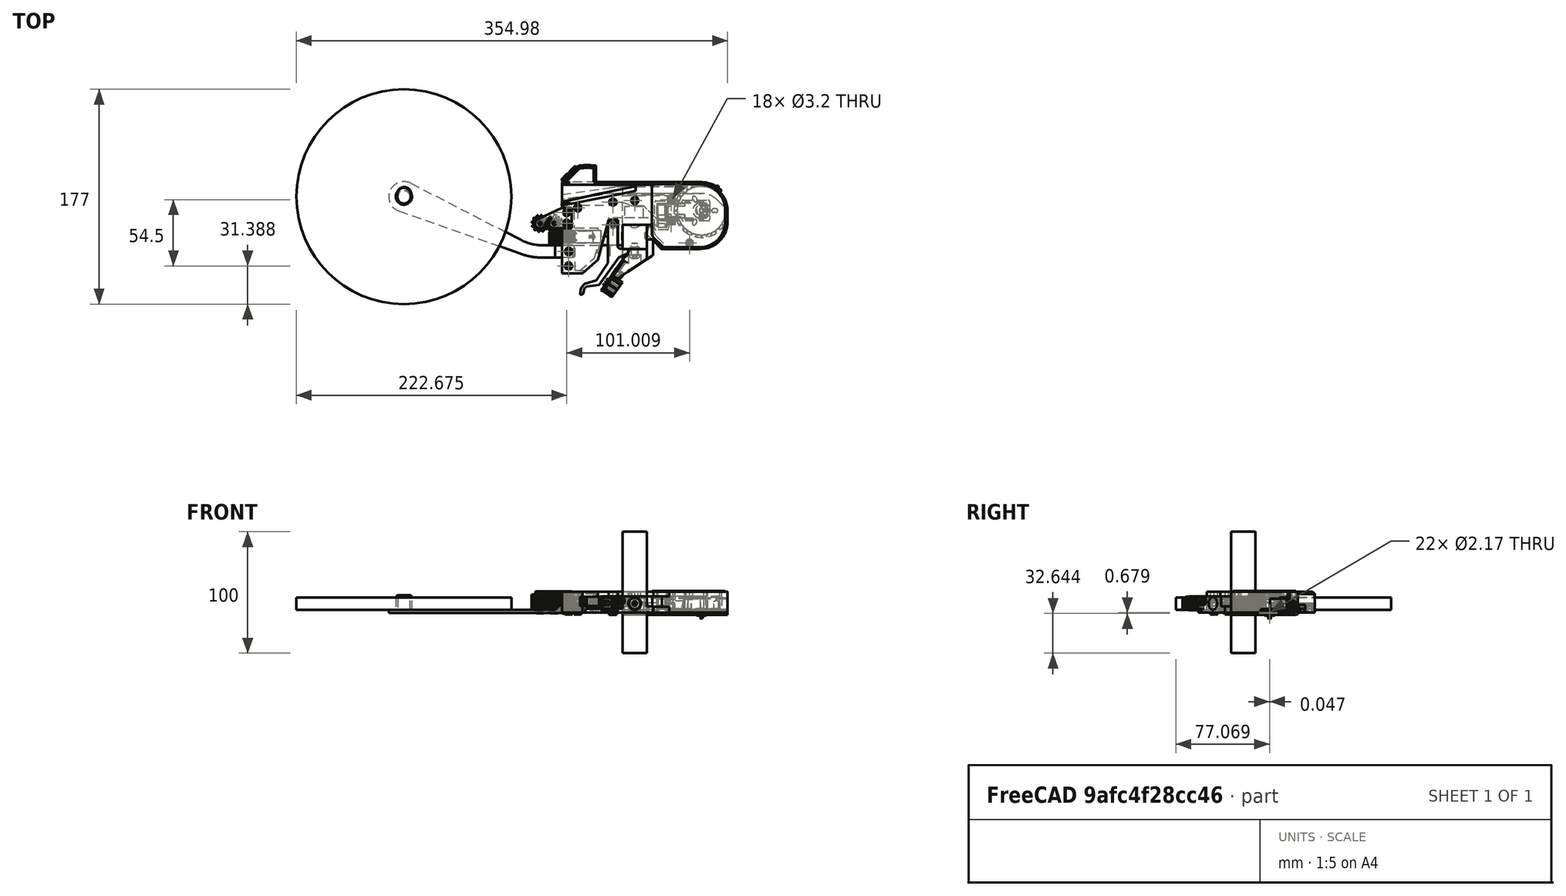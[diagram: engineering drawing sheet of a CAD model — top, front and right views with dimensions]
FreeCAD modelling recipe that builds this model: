
FCSTD DOCUMENT  (FreeCAD 0.20R29603 (Git))
Label: asm
License: All rights reserved
LicenseURL: http://en.wikipedia.org/wiki/All_rights_reserved
objects: Part::FeaturePython×80, PartDesign::CoordinateSystem×29, App::Part×1
note: 109 computed .brp shape members not serialized (recipe doc carries the construction recipe); baked Part::Feature solids carry a one-line shape summary decoded from their .brp

FEATURE [Part::FeaturePython] b_rail_001_  label="rail_Body_001"  # a2plus imported part (geometry in sourceFile) (typed FeaturePython)
  Placement = pos=(132.29,-99.02,-33.33) rot=(-1,0,0;1.5708rad)
  a2p_Version = V0.1
  fixedPosition = true
  objectType = a2pPart
  sourceFile = ./rail.FCStd
  sourcePart = Body
  subassemblyImport = false
  timeLastImport = 1.65956e+09
  updateColors = true
FEATURE [PartDesign::CoordinateSystem] a2pLCS
  AttacherType = Attacher::AttachEngine3D
FEATURE [Part::FeaturePython] b_LCS_Collection_  label="LCS_Collection"  # WARN: FeaturePython — macro-defined, semantics opaque (R4)
  Group = -> [a2pLCS]
  Owner = b_feederFloorPCB_001_
  Placement = pos=(148.005,-87.9308,34.6832) rot=(0.287968,0.913318,-0.287968;1.66134rad)
FEATURE [Part::FeaturePython] b_feederFloorPCB_001_  label="feederFloorPCB_001"  # a2plus imported part (geometry in sourceFile) (typed FeaturePython)
  Placement = pos=(148.005,-87.9308,34.6832) rot=(0.287968,0.913318,-0.287968;1.66134rad)
  a2p_Version = V0.1
  fixedPosition = false
  lcsLink = -> [b_LCS_Collection_]
  objectType = a2pPart
  sourceFile = ./feederFloorPCB.FCStd
  subassemblyImport = false
  timeLastImport = 1.67053e+09
  updateColors = true
FEATURE [Part::FeaturePython] b_frame_001_  label="frame_Body_001"  # a2plus imported part (geometry in sourceFile) (typed FeaturePython)
  Placement = pos=(132.339,-79.0017,-1.65661) rot=(-1,0,0;1.5708rad)
  a2p_Version = 0.4.60i
  fixedPosition = false
  objectType = a2pPart
  sourceFile = ./frame.FCStd
  sourcePart = Body
  subassemblyImport = false
  timeLastImport = 1.68014e+09
  updateColors = true
FEATURE [Part::FeaturePython] b_railLock_001_  label="railLock_Body_001"  # a2plus imported part (geometry in sourceFile) (typed FeaturePython)
  Placement = pos=(128.216,-75.0366,5.45816) rot=(-1,0,0;1.5708rad)
  a2p_Version = V0.1
  fixedPosition = false
  objectType = a2pPart
  sourceFile = ./railLock.FCStd
  sourcePart = Body
  subassemblyImport = false
  timeLastImport = 1.66559e+09
  updateColors = true
FEATURE [Part::FeaturePython] Screw  label="M5x10-Screw"  # Fasteners workbench fastener (typed FeaturePython)
  Placement = pos=(142.2,-104.2,7.5) rot=(1,0,0;1.5708rad)
  diameter = 3
  invert = false
  leftHanded = false
  length = 1
  lengthCustom = 10
  matchOuter = false
  offset = 0
  thread = false
  type = 40
FEATURE [PartDesign::CoordinateSystem] a2pLCS022
  AttacherType = Attacher::AttachEngine3D
FEATURE [Part::FeaturePython] b_LCS_Collection_022  label="LCS_Collection022"  # WARN: FeaturePython — macro-defined, semantics opaque (R4)
  Group = -> [a2pLCS022]
  Owner = b_controllerPCB_001_
  Placement = pos=(0.0377435,-0.00241684,-0.0301529) rot=(0,0,1;0rad)
FEATURE [Part::FeaturePython] b_controllerPCB_001_  label="controllerPCB_001"  # a2plus imported part (geometry in sourceFile) (typed FeaturePython)
  Placement = pos=(0.0377435,-0.00241684,-0.0301529) rot=(0,0,1;0rad)
  a2p_Version = V0.1
  fixedPosition = false
  lcsLink = -> [b_LCS_Collection_022]
  objectType = a2pPart
  sourceFile = ./controllerPCB.FCStd
  subassemblyImport = false
  timeLastImport = 1.67242e+09
  updateColors = true
FEATURE [App::Part] Part
  Group = -> [b_LCS_Collection_022,b_controllerPCB_001_,b_frame_001_]
  Origin = -> Origin
FEATURE [PartDesign::CoordinateSystem] a2pLCS023
  AttacherType = Attacher::AttachEngine3D
FEATURE [Part::FeaturePython] b_LCS_Collection_023  label="LCS_Collection023"  # WARN: FeaturePython — macro-defined, semantics opaque (R4)
  Group = -> [a2pLCS023]
  Owner = CachedObject_0
FEATURE [Part::FeaturePython] b_feeder_floor_001_001  label="feeder-floor_Body_001"  # a2plus imported part (geometry in sourceFile) (typed FeaturePython)
  Placement = pos=(152.293,-99.0214,-0.00814896) rot=(0,0,1;0rad)
  a2p_Version = V0.1
  fixedPosition = false
  objectType = a2pPart
  sourceFile = ./feeder-floor.FCStd
  sourcePart = Body
  subassemblyImport = false
  timeLastImport = 1.67053e+09
  updateColors = true
FEATURE [PartDesign::CoordinateSystem] a2pLCS024
  AttacherType = Attacher::AttachEngine3D
FEATURE [Part::FeaturePython] b_LCS_Collection_024  label="LCS_Collection024"  # WARN: FeaturePython — macro-defined, semantics opaque (R4)
  Group = -> [a2pLCS024]
  Owner = CachedObject_0
FEATURE [PartDesign::CoordinateSystem] a2pLCS025
  AttacherType = Attacher::AttachEngine3D
FEATURE [Part::FeaturePython] b_LCS_Collection_025  label="LCS_Collection025"  # WARN: FeaturePython — macro-defined, semantics opaque (R4)
  Group = -> [a2pLCS025]
  Owner = CachedObject_0
FEATURE [PartDesign::CoordinateSystem] a2pLCS026
  AttacherType = Attacher::AttachEngine3D
FEATURE [Part::FeaturePython] b_LCS_Collection_026  label="LCS_Collection026"  # WARN: FeaturePython — macro-defined, semantics opaque (R4)
  Group = -> [a2pLCS026]
  Owner = CachedObject_0
FEATURE [PartDesign::CoordinateSystem] a2pLCS027
  AttacherType = Attacher::AttachEngine3D
FEATURE [Part::FeaturePython] b_LCS_Collection_027  label="LCS_Collection027"  # WARN: FeaturePython — macro-defined, semantics opaque (R4)
  Group = -> [a2pLCS027]
  Owner = CachedObject_0
FEATURE [PartDesign::CoordinateSystem] a2pLCS028
  AttacherType = Attacher::AttachEngine3D
FEATURE [Part::FeaturePython] b_LCS_Collection_028  label="LCS_Collection028"  # WARN: FeaturePython — macro-defined, semantics opaque (R4)
  Group = -> [a2pLCS028]
  Owner = CachedObject_0
FEATURE [Part::FeaturePython] Nut  label="M3-Nut"  # Fasteners workbench fastener (typed FeaturePython)
  Placement = pos=(129.317,-119.93,9.48) rot=(0.287968,0.913318,-0.287968;1.66134rad)
  diameter = 4
  invert = false
  leftHanded = false
  matchOuter = false
  offset = 0
  thread = false
  type = 7
FEATURE [PartDesign::CoordinateSystem] a2pLCS029
  AttacherType = Attacher::AttachEngine3D
FEATURE [Part::FeaturePython] b_LCS_Collection_029  label="LCS_Collection029"  # WARN: FeaturePython — macro-defined, semantics opaque (R4)
  Group = -> [a2pLCS029]
  Owner = CachedObject_0
FEATURE [PartDesign::CoordinateSystem] a2pLCS030
  AttacherType = Attacher::AttachEngine3D
FEATURE [Part::FeaturePython] b_LCS_Collection_030  label="LCS_Collection030"  # WARN: FeaturePython — macro-defined, semantics opaque (R4)
  Group = -> [a2pLCS030]
  Owner = CachedObject_0
FEATURE [PartDesign::CoordinateSystem] a2pLCS031
  AttacherType = Attacher::AttachEngine3D
FEATURE [Part::FeaturePython] b_LCS_Collection_031  label="LCS_Collection031"  # WARN: FeaturePython — macro-defined, semantics opaque (R4)
  Group = -> [a2pLCS031]
  Owner = CachedObject_0
FEATURE [PartDesign::CoordinateSystem] a2pLCS032
  AttacherType = Attacher::AttachEngine3D
FEATURE [Part::FeaturePython] b_LCS_Collection_032  label="LCS_Collection032"  # WARN: FeaturePython — macro-defined, semantics opaque (R4)
  Group = -> [a2pLCS032]
  Owner = CachedObject_0
FEATURE [PartDesign::CoordinateSystem] a2pLCS033
  AttacherType = Attacher::AttachEngine3D
FEATURE [Part::FeaturePython] b_LCS_Collection_033  label="LCS_Collection033"  # WARN: FeaturePython — macro-defined, semantics opaque (R4)
  Group = -> [a2pLCS033]
  Owner = CachedObject_0
FEATURE [PartDesign::CoordinateSystem] a2pLCS034
  AttacherType = Attacher::AttachEngine3D
FEATURE [Part::FeaturePython] b_LCS_Collection_034  label="LCS_Collection034"  # WARN: FeaturePython — macro-defined, semantics opaque (R4)
  Group = -> [a2pLCS034]
  Owner = CachedObject_0
FEATURE [PartDesign::CoordinateSystem] a2pLCS035
  AttacherType = Attacher::AttachEngine3D
FEATURE [Part::FeaturePython] b_LCS_Collection_035  label="LCS_Collection035"  # WARN: FeaturePython — macro-defined, semantics opaque (R4)
  Group = -> [a2pLCS035]
  Owner = CachedObject_0
FEATURE [PartDesign::CoordinateSystem] a2pLCS036
  AttacherType = Attacher::AttachEngine3D
FEATURE [Part::FeaturePython] b_LCS_Collection_036  label="LCS_Collection036"  # WARN: FeaturePython — macro-defined, semantics opaque (R4)
  Group = -> [a2pLCS036]
  Owner = CachedObject_0
FEATURE [Part::FeaturePython] b_spool_holder_001_  label="spool-holder_Body_001"  # a2plus imported part (geometry in sourceFile) (typed FeaturePython)
  Placement = pos=(92.2739,-106.017,2.19804) rot=(0,0,1;0rad)
  a2p_Version = V0.1
  fixedPosition = false
  objectType = a2pPart
  sourceFile = ./spool-holder.FCStd
  sourcePart = Body
  subassemblyImport = false
  timeLastImport = 1.67476e+09
  updateColors = true
FEATURE [Part::FeaturePython] b_spool_001_  label="spool_Body_001"  # a2plus imported part (geometry in sourceFile) (typed FeaturePython)
  Placement = pos=(-47.8234,-55.8871,2.36078) rot=(0,0,1;0rad)
  a2p_Version = V0.1
  fixedPosition = false
  objectType = a2pPart
  sourceFile = ./spool.FCStd
  sourcePart = Body
  subassemblyImport = false
  timeLastImport = 1.66558e+09
  updateColors = true
FEATURE [Part::FeaturePython] b_film_gear_frame_001_001  label="film-gear-frame_Body_002"  # a2plus imported part (geometry in sourceFile) (typed FeaturePython)
  Placement = pos=(64.3546,-77.9852,17.3599) rot=(0.57735,0.57735,0.57735;4.18879rad)
  a2p_Version = 0.4.60i
  fixedPosition = false
  objectType = a2pPart
  sourceFile = ./film-gear-frame.FCStd
  sourcePart = Body
  subassemblyImport = false
  timeLastImport = 1.68013e+09
  updateColors = true
FEATURE [Part::FeaturePython] b_drive_motor_bracket_001_  label="drive-motor-bracket_Body_001"  # a2plus imported part (geometry in sourceFile) (typed FeaturePython)
  Placement = pos=(175.069,-78.8015,1.90918) rot=(0.707107,0.707107,0;3.14159rad)
  a2p_Version = V0.1
  fixedPosition = false
  objectType = a2pPart
  sourceFile = ./drive-motor-bracket.FCStd
  sourcePart = Body
  subassemblyImport = false
  timeLastImport = 1.67476e+09
  updateColors = true
FEATURE [Part::FeaturePython] b_drive_motor_cover_001_  label="drive-motor-cover_Body_001"  # a2plus imported part (geometry in sourceFile) (typed FeaturePython)
  Placement = pos=(132.364,-79.0154,-1.70701) rot=(-1,0,0;1.5708rad)
  a2p_Version = V0.1
  fixedPosition = false
  objectType = a2pPart
  sourceFile = ./drive-motor-cover.FCStd
  sourcePart = Body
  subassemblyImport = false
  timeLastImport = 1.67475e+09
  updateColors = true
FEATURE [Part::FeaturePython] b_right_angle_n20_001_  label="right-angle-n20_Body_001"  # a2plus imported part (geometry in sourceFile) (typed FeaturePython)
  Placement = pos=(197.308,-67.2968,3.38748) rot=(0.707107,0.707107,0;3.14159rad)
  a2p_Version = V0.1
  fixedPosition = false
  objectType = a2pPart
  sourceFile = ./right-angle-n20.FCStd
  sourcePart = Body
  subassemblyImport = false
  timeLastImport = 1.6668e+09
  updateColors = true
FEATURE [Part::FeaturePython] b_peel_gear_001_  label="peel-gear_Body_001"  # a2plus imported part (geometry in sourceFile) (typed FeaturePython)
  Placement = pos=(75.8569,-77.9542,14.8915) rot=(0.034899,0.999391,0;3.14159rad)
  a2p_Version = 0.4.60i
  fixedPosition = false
  objectType = a2pPart
  sourceFile = ./peel-gear.FCStd
  sourcePart = Body
  subassemblyImport = false
  timeLastImport = 1.68013e+09
  updateColors = true
FEATURE [Part::FeaturePython] b_peel_gear_001_001  label="peel-gear_Body_002"  # a2plus imported part (geometry in sourceFile) (typed FeaturePython)
  Placement = pos=(64.342,-77.973,14.939) rot=(0.087156,0.996195,0;3.14159rad)
  a2p_Version = 0.4.60i
  fixedPosition = false
  objectType = a2pPart
  sourceFile = ./peel-gear.FCStd
  sourcePart = Body
  subassemblyImport = false
  timeLastImport = 1.68013e+09
  updateColors = true
FEATURE [PartDesign::CoordinateSystem] a2pLCS037
  AttacherType = Attacher::AttachEngine3D
FEATURE [Part::FeaturePython] b_LCS_Collection_037  label="LCS_Collection037"  # WARN: FeaturePython — macro-defined, semantics opaque (R4)
  Group = -> [a2pLCS037]
  Owner = CachedObject_1
FEATURE [PartDesign::CoordinateSystem] a2pLCS038
  AttacherType = Attacher::AttachEngine3D
FEATURE [Part::FeaturePython] b_LCS_Collection_038  label="LCS_Collection038"  # WARN: FeaturePython — macro-defined, semantics opaque (R4)
  Group = -> [a2pLCS038]
  Owner = CachedObject_0
FEATURE [PartDesign::CoordinateSystem] a2pLCS039
  AttacherType = Attacher::AttachEngine3D
FEATURE [Part::FeaturePython] b_LCS_Collection_039  label="LCS_Collection039"  # WARN: FeaturePython — macro-defined, semantics opaque (R4)
  Group = -> [a2pLCS039]
  Owner = CachedObject_1
FEATURE [Part::FeaturePython] b_diffusor_001_  label="diffusor_Body_001"  # a2plus imported part (geometry in sourceFile) (typed FeaturePython)
  Placement = pos=(100.03,-30.0449,-0.0241241) rot=(0,0,1;0rad)
  a2p_Version = V0.1
  fixedPosition = false
  objectType = a2pPart
  sourceFile = ./diffusor.FCStd
  sourcePart = Body
  subassemblyImport = false
  timeLastImport = 1.67001e+09
  updateColors = true
FEATURE [PartDesign::CoordinateSystem] a2pLCS040
  AttacherType = Attacher::AttachEngine3D
FEATURE [Part::FeaturePython] b_LCS_Collection_040  label="LCS_Collection040"  # WARN: FeaturePython — macro-defined, semantics opaque (R4)
  Group = -> [a2pLCS040]
  Owner = CachedObject_0
FEATURE [PartDesign::CoordinateSystem] a2pLCS041
  AttacherType = Attacher::AttachEngine3D
FEATURE [Part::FeaturePython] b_LCS_Collection_041  label="LCS_Collection041"  # WARN: FeaturePython — macro-defined, semantics opaque (R4)
  Group = -> [a2pLCS041]
  Owner = CachedObject_0
FEATURE [PartDesign::CoordinateSystem] a2pLCS042
  AttacherType = Attacher::AttachEngine3D
FEATURE [Part::FeaturePython] b_LCS_Collection_042  label="LCS_Collection042"  # WARN: FeaturePython — macro-defined, semantics opaque (R4)
  Group = -> [a2pLCS042]
  Owner = CachedObject_0
FEATURE [PartDesign::CoordinateSystem] a2pLCS043
  AttacherType = Attacher::AttachEngine3D
FEATURE [Part::FeaturePython] b_LCS_Collection_043  label="LCS_Collection043"  # WARN: FeaturePython — macro-defined, semantics opaque (R4)
  Group = -> [a2pLCS043]
  Owner = CachedObject_0
FEATURE [PartDesign::CoordinateSystem] a2pLCS044
  AttacherType = Attacher::AttachEngine3D
FEATURE [Part::FeaturePython] b_LCS_Collection_044  label="LCS_Collection044"  # WARN: FeaturePython — macro-defined, semantics opaque (R4)
  Group = -> [a2pLCS044]
  Owner = CachedObject_1
FEATURE [PartDesign::CoordinateSystem] a2pLCS045
  AttacherType = Attacher::AttachEngine3D
FEATURE [Part::FeaturePython] b_LCS_Collection_045  label="LCS_Collection045"  # WARN: FeaturePython — macro-defined, semantics opaque (R4)
  Group = -> [a2pLCS045]
  Owner = b_indexing_wheel_pcb_001_
  Placement = pos=(290.162,82.0768,2.59864) rot=(0,0,-1;1.5708rad)
FEATURE [Part::FeaturePython] b_indexing_wheel_pcb_001_  label="indexing-wheel-pcb_Pcb_6bbf_001"  # a2plus imported part (geometry in sourceFile) (typed FeaturePython)
  Placement = pos=(290.162,82.0768,2.59864) rot=(0,0,-1;1.5708rad)
  a2p_Version = V0.1
  fixedPosition = false
  lcsLink = -> [b_LCS_Collection_045]
  objectType = a2pPart
  sourceFile = <userpath>/Github/feeder/cad/indexing-wheel.FCStd
  sourcePart = Pcb_6bbf
  subassemblyImport = false
  timeLastImport = 1.67053e+09
  updateColors = true
FEATURE [Part::FeaturePython] b_shaft_collar_001_  label="shaft-collar_Body_001"  # a2plus imported part (geometry in sourceFile) (typed FeaturePython)
  Placement = pos=(197.288,-67.2733,0.964391) rot=(0.707107,0.707107,0;3.14159rad)
  a2p_Version = 0.4.60i
  fixedPosition = false
  objectType = a2pPart
  sourceFile = ./shaft-collar.FCStd
  sourcePart = Body
  subassemblyImport = false
  timeLastImport = 1.67648e+09
  updateColors = true
FEATURE [Part::FeaturePython] Screw001  label="M3x8-Screw"  # Fasteners workbench fastener (typed FeaturePython)
  Placement = pos=(125.341,-117.14,9.5) rot=(-0.287968,-0.913318,-0.287968;1.66134rad)
  diameter = 3
  invert = false
  leftHanded = false
  length = 0
  lengthCustom = 8
  matchOuter = false
  offset = 0
  thread = false
  type = 18
FEATURE [PartDesign::CoordinateSystem] a2pLCS046
  AttacherType = Attacher::AttachEngine3D
FEATURE [Part::FeaturePython] b_LCS_Collection_046  label="LCS_Collection046"  # WARN: FeaturePython — macro-defined, semantics opaque (R4)
  Group = -> [a2pLCS046]
  Owner = CachedObject_0
FEATURE [Part::FeaturePython] Screw002  label="M3x12-Screw"  # Fasteners workbench fastener (typed FeaturePython)
  Placement = pos=(172.3,-58.5,1.06) rot=(1,0,0;3.14159rad)
  diameter = 3
  invert = false
  leftHanded = false
  length = 2
  lengthCustom = 12
  matchOuter = false
  offset = 0
  thread = false
  type = 18
FEATURE [Part::FeaturePython] Screw003  label="M3x12-Screw001"  # Fasteners workbench fastener (typed FeaturePython)
  Placement = pos=(172.3,-76,0.8) rot=(1,0,0;3.14159rad)
  diameter = 3
  invert = false
  leftHanded = false
  length = 2
  lengthCustom = 12
  matchOuter = false
  offset = 0
  thread = false
  type = 18
FEATURE [PartDesign::CoordinateSystem] a2pLCS047
  AttacherType = Attacher::AttachEngine3D
FEATURE [Part::FeaturePython] b_LCS_Collection_047  label="LCS_Collection047"  # WARN: FeaturePython — macro-defined, semantics opaque (R4)
  Group = -> [a2pLCS047]
  Owner = CachedObject_0
FEATURE [PartDesign::CoordinateSystem] a2pLCS048
  AttacherType = Attacher::AttachEngine3D
FEATURE [Part::FeaturePython] b_LCS_Collection_048  label="LCS_Collection048"  # WARN: FeaturePython — macro-defined, semantics opaque (R4)
  Group = -> [a2pLCS048]
  Owner = CachedObject_1
FEATURE [Part::FeaturePython] b_peel_worm_gear_001_  label="peel-worm-gear_001"  # a2plus imported part (geometry in sourceFile) (typed FeaturePython)
  Placement = pos=(82.0039,-88.9703,5.994) rot=(0,-1,0;1.5708rad)
  a2p_Version = V0.1
  fixedPosition = false
  objectType = a2pPart
  sourceFile = ./peel-worm-gear.FCStd
  subassemblyImport = false
  timeLastImport = 1.67527e+09
  updateColors = true
FEATURE [Part::FeaturePython] b_n20_motor_001_  label="n20-motor_001"  # a2plus imported part (geometry in sourceFile) (typed FeaturePython)
  Placement = pos=(92.3805,-88.9618,5.98278) rot=(0,-1,0;1.5708rad)
  a2p_Version = V0.1
  fixedPosition = false
  objectType = a2pPart
  sourceFile = ./n20-motor.FCStd
  subassemblyImport = false
  timeLastImport = 1.65481e+09
  updateColors = true
FEATURE [PartDesign::CoordinateSystem] a2pLCS049
  AttacherType = Attacher::AttachEngine3D
FEATURE [Part::FeaturePython] b_LCS_Collection_049  label="LCS_Collection049"  # WARN: FeaturePython — macro-defined, semantics opaque (R4)
  Group = -> [a2pLCS049]
  Owner = b_photon_8mm_fidPCB_001_
  Placement = pos=(207.343,-46.0196,-0.0534958) rot=(-0.57735,-0.57735,-0.57735;2.0944rad)
FEATURE [Part::FeaturePython] b_photon_8mm_fidPCB_001_  label="photon-8mm-fidPCB_001"  # a2plus imported part (geometry in sourceFile) (typed FeaturePython)
  Placement = pos=(207.343,-46.0196,-0.0534958) rot=(0.57735,0.57735,0.57735;4.18879rad)
  a2p_Version = V0.1
  fixedPosition = false
  lcsLink = -> [b_LCS_Collection_049]
  objectType = a2pPart
  sourceFile = ./photon-8mm-fidPCB.FCStd
  subassemblyImport = false
  timeLastImport = 1.67588e+09
  updateColors = true
FEATURE [Part::FeaturePython] Screw004  label="M3x18-Screw"  # Fasteners workbench fastener (typed FeaturePython)
  Placement = pos=(75.86,-77.99,-0.55) rot=(0,1,0;3.14159rad)
  diameter = 3
  invert = false
  leftHanded = false
  length = 7
  lengthCustom = 18
  matchOuter = false
  offset = 0
  thread = false
  type = 18
FEATURE [Part::FeaturePython] Screw005  label="M3x18-Screw001"  # Fasteners workbench fastener (typed FeaturePython)
  Placement = pos=(64.39,-77.99,-0.55) rot=(0,1,0;3.14159rad)
  diameter = 3
  invert = false
  leftHanded = false
  length = 7
  lengthCustom = 18
  matchOuter = false
  offset = 0
  thread = false
  type = 18
FEATURE [Part::FeaturePython] Screw006  label="M3x15-Screw"  # Fasteners workbench fastener (typed FeaturePython)
  Placement = pos=(124.35,-60.5,-1.67) rot=(0,1,0;3.14159rad)
  diameter = 3
  invert = false
  leftHanded = false
  length = 7
  lengthCustom = 15
  matchOuter = false
  offset = 0
  thread = false
  type = 18
FEATURE [Part::FeaturePython] Screw007  label="M3x15-Screw003"  # Fasteners workbench fastener (typed FeaturePython)
  Placement = pos=(142.35,-59.01,-1.75) rot=(0,1,0;3.14159rad)
  diameter = 3
  invert = false
  leftHanded = false
  length = 7
  lengthCustom = 15
  matchOuter = false
  offset = 0
  thread = false
  type = 18
FEATURE [Part::FeaturePython] Screw008  label="M3x15-Screw002"  # Fasteners workbench fastener (typed FeaturePython)
  Placement = pos=(124.19,-79.06,-1.7) rot=(0,1,0;3.14159rad)
  diameter = 3
  invert = false
  leftHanded = false
  length = 7
  lengthCustom = 15
  matchOuter = false
  offset = 0
  thread = false
  type = 18
FEATURE [Part::FeaturePython] Screw009  label="M3x15-Screw004"  # Fasteners workbench fastener (typed FeaturePython)
  Placement = pos=(95.33,-65,-1.67) rot=(0,1,0;3.14159rad)
  diameter = 3
  invert = false
  leftHanded = false
  length = 7
  lengthCustom = 15
  matchOuter = false
  offset = 0
  thread = false
  type = 18
FEATURE [Part::FeaturePython] Screw010  label="M3x15-Screw010"  # Fasteners workbench fastener (typed FeaturePython)
  Placement = pos=(86.35,-68.99,-1.67) rot=(0,1,0;3.14159rad)
  diameter = 3
  invert = false
  leftHanded = false
  length = 7
  lengthCustom = 15
  matchOuter = false
  offset = 0
  thread = false
  type = 18
FEATURE [Part::FeaturePython] Screw011  label="M3x15-Screw011"  # Fasteners workbench fastener (typed FeaturePython)
  Placement = pos=(86.35,-78,-1.67) rot=(0,1,0;3.14159rad)
  diameter = 3
  invert = false
  leftHanded = false
  length = 7
  lengthCustom = 15
  matchOuter = false
  offset = 0
  thread = false
  type = 18
FEATURE [Part::FeaturePython] Screw012  label="M3x15-Screw007"  # Fasteners workbench fastener (typed FeaturePython)
  Placement = pos=(87.86,-101.01,-1.67) rot=(0,1,0;3.14159rad)
  diameter = 3
  invert = false
  leftHanded = false
  length = 7
  lengthCustom = 15
  matchOuter = false
  offset = 0
  thread = false
  type = 18
FEATURE [Part::FeaturePython] Screw013  label="M3x15-Screw008"  # Fasteners workbench fastener (typed FeaturePython)
  Placement = pos=(87.86,-112.99,-1.67) rot=(0,1,0;3.14159rad)
  diameter = 3
  invert = false
  leftHanded = false
  length = 7
  lengthCustom = 15
  matchOuter = false
  offset = 0
  thread = false
  type = 18
FEATURE [Part::FeaturePython] Screw014  label="M3x15-Screw009"  # Fasteners workbench fastener (typed FeaturePython)
  Placement = pos=(187.33,-94.01,-1.75) rot=(0,1,0;3.14159rad)
  diameter = 3
  invert = false
  leftHanded = false
  length = 7
  lengthCustom = 15
  matchOuter = false
  offset = 0
  thread = false
  type = 18
FEATURE [Part::FeaturePython] Nut001  label="M3-Nut001"  # Fasteners workbench fastener (typed FeaturePython)
  Placement = pos=(172.35,-58.5,10.98) rot=(0,0,1;0rad)
  diameter = 4
  invert = false
  leftHanded = false
  matchOuter = false
  offset = 0
  thread = false
  type = 7
FEATURE [Part::FeaturePython] Nut002  label="M3-Nut002"  # Fasteners workbench fastener (typed FeaturePython)
  Placement = pos=(172.35,-76.1,10.98) rot=(0,0,1;0rad)
  diameter = 4
  invert = false
  leftHanded = false
  matchOuter = false
  offset = 0
  thread = false
  type = 7
FEATURE [Part::FeaturePython] Nut003  label="M3-Nut003"  # Fasteners workbench fastener (typed FeaturePython)
  Placement = pos=(142.367,-58.9951,10.98) rot=(0,0,-1;0.523599rad)
  diameter = 4
  invert = false
  leftHanded = false
  matchOuter = false
  offset = 0
  thread = false
  type = 7
FEATURE [Part::FeaturePython] Nut004  label="M3-Nut004"  # Fasteners workbench fastener (typed FeaturePython)
  Placement = pos=(124.371,-60.4865,10.98) rot=(0,0,-1;0.523599rad)
  diameter = 4
  invert = false
  leftHanded = false
  matchOuter = false
  offset = 0
  thread = false
  type = 7
FEATURE [Part::FeaturePython] Nut005  label="M3-Nut005"  # Fasteners workbench fastener (typed FeaturePython)
  Placement = pos=(95.3647,-64.9863,10.98) rot=(0,0,-1;0.523599rad)
  diameter = 4
  invert = false
  leftHanded = false
  matchOuter = false
  offset = 0
  thread = false
  type = 7
FEATURE [Part::FeaturePython] Nut006  label="M3-Nut006"  # Fasteners workbench fastener (typed FeaturePython)
  Placement = pos=(86.3617,-68.9799,10.98) rot=(0,0,-1;0.523599rad)
  diameter = 4
  invert = false
  leftHanded = false
  matchOuter = false
  offset = 0
  thread = false
  type = 7
FEATURE [Part::FeaturePython] Nut007  label="M3-Nut007"  # Fasteners workbench fastener (typed FeaturePython)
  Placement = pos=(86.3712,-78.0036,10.98) rot=(0,0,-1;0.523599rad)
  diameter = 4
  invert = false
  leftHanded = false
  matchOuter = false
  offset = 0
  thread = false
  type = 7
FEATURE [Part::FeaturePython] Nut008  label="M3-Nut008"  # Fasteners workbench fastener (typed FeaturePython)
  Placement = pos=(87.8096,-101.011,10.98) rot=(0,0,1;0rad)
  diameter = 4
  invert = false
  leftHanded = false
  matchOuter = false
  offset = 0
  thread = false
  type = 7
FEATURE [Part::FeaturePython] Nut009  label="M3-Nut009"  # Fasteners workbench fastener (typed FeaturePython)
  Placement = pos=(87.8096,-113.001,10.98) rot=(0,0,1;0rad)
  diameter = 4
  invert = false
  leftHanded = false
  matchOuter = false
  offset = 0
  thread = false
  type = 7
FEATURE [Part::FeaturePython] Nut010  label="M3-Nut010"  # Fasteners workbench fastener (typed FeaturePython)
  Placement = pos=(187.356,-94.0334,10.98) rot=(0,0,-1;0.523599rad)
  diameter = 4
  invert = false
  leftHanded = false
  matchOuter = false
  offset = 0
  thread = false
  type = 7
FEATURE [Part::FeaturePython] b_shaft_collar_001_001  label="shaft-collar_Body_002"  # a2plus imported part (geometry in sourceFile) (typed FeaturePython)
  Placement = pos=(197.308,-67.2968,1.64364) rot=(0.708398,0.705813,0;3.14159rad)
  a2p_Version = 0.4.60i
  fixedPosition = true
  objectType = a2pPart
  sourceFile = <userpath>/Github/feeder/cad/shaft-collar.FCStd
  sourcePart = Body
  subassemblyImport = false
  timeLastImport = 1.67648e+09
  updateColors = true
FEATURE [Part::FeaturePython] b_indexing_wheel_001_  label="indexing-wheel_001"  # a2plus imported part (geometry in sourceFile) (typed FeaturePython)
  Placement = pos=(197.308,-67.2968,1.64365) rot=(0,0,1;0rad)
  a2p_Version = 0.4.60i
  fixedPosition = true
  objectType = a2pPart
  sourceFile = ./indexing-wheel.FCStd
  subassemblyImport = false
  timeLastImport = 1.67649e+09
  updateColors = true
FEATURE [Part::FeaturePython] b_90358A111_Ultra_Low_Profile_Socket_Head_Screw1_001_  label="90358A111_Ultra-Low-Profile Socket Head Screw1_001"  # a2plus imported part (geometry in sourceFile) (typed FeaturePython)
  Placement = pos=(197.292,-71.5592,0.0436583) rot=(0,1,0;3.14159rad)
  a2p_Version = 0.4.60i
  fixedPosition = false
  objectType = a2pPart
  sourceFile = <userpath>/Github/feeder/cad/M2.5x4-ultra-low-profile-socket-head-bolt.FCStd
  subassemblyImport = false
  timeLastImport = 1.67649e+09
  updateColors = true
FEATURE [Part::FeaturePython] b_90358A111_Ultra_Low_Profile_Socket_Head_Screw1_001_001  label="90358A111_Ultra-Low-Profile Socket Head Screw1_002"  # a2plus imported part (geometry in sourceFile) (typed FeaturePython)
  Placement = pos=(197.323,-63.0343,0.0436552) rot=(0,1,0;3.14159rad)
  a2p_Version = 0.4.60i
  fixedPosition = false
  objectType = a2pPart
  sourceFile = <userpath>/Github/feeder/cad/M2.5x4-ultra-low-profile-socket-head-bolt.FCStd
  subassemblyImport = false
  timeLastImport = 1.67649e+09
  updateColors = true
FEATURE [Part::FeaturePython] b_sticker_8mm_001_  label="sticker-8mm_001"  # a2plus imported part (geometry in sourceFile) (typed FeaturePython)
  Placement = pos=(132,-79,17.345) rot=(0,0,1;0rad)
  a2p_Version = 0.4.60i
  fixedPosition = false
  objectType = a2pPart
  sourceFile = ./sticker-8mm.FCStd
  subassemblyImport = false
  timeLastImport = 1.67933e+09
  updateColors = true
